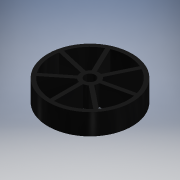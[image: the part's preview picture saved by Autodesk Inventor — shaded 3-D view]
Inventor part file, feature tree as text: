
AUTODESK INVENTOR PART (.ipt)
format: ipt  version: 2017 SP1 (Build 210196100, 196)  size: 154,112 bytes
history: native  units: in
note: dims shown in document units (in); Inventor stores cm internally (conversion verified against a paired STEP export)
features: extrude x1, sketch x1
ambient origin geometry x8: Origin, YZ Plane, XZ Plane, XY Plane, X Axis, Y Axis, Z Axis, Center Point
bodies: Solid1 (feature_tree)
feature tree (2):
  extrude  "Extrusion1"  Depth=0.1875in
  sketch  "Sketch1"  dims[d0=0.5in d1=4.0in d2=1.0in d3=0.0in d4=0.1875in d5=0.1875in d6=2.7559in d8=360.0deg d10=0.1875in]
